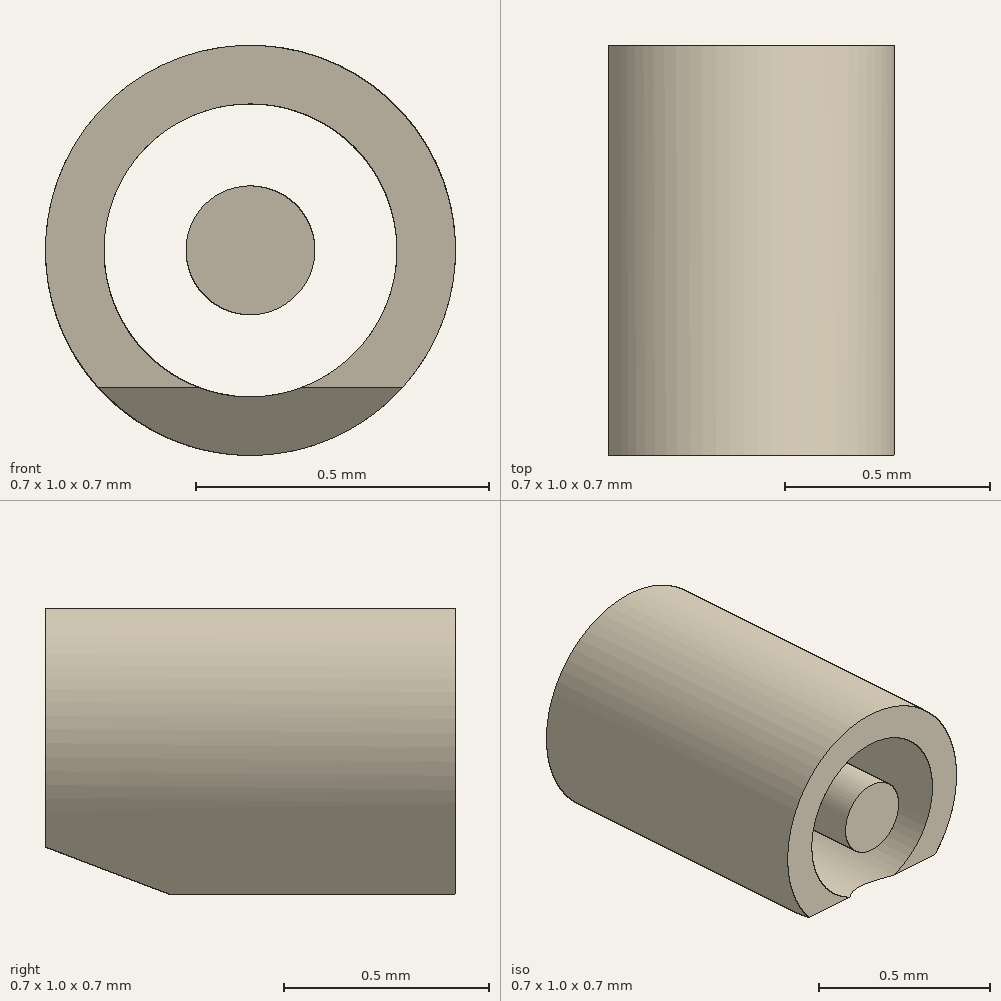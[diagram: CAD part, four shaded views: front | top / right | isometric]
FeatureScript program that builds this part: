
annotation { "Feature Type Name" : "Feature", "Feature Type Description" : "" }
export const myFeature = defineFeature(function(context is Context, id is Id, definition is map)
    precondition{}
    {
        {
            var Q0;
            Q0=qCreatedBy(makeId("Front.planeOp"),FACE);
            var sketch = newSketch(context, id + "F0", { "sketchPlane" : qUnion([Q0])});
            skCircle(sketch, "E0", {"center": v(0, 0) * mm, "radius": 0.11 * mm});
            skCircle(sketch, "E1", {"center": v(0, 0) * mm, "radius": 0.25 * mm});
            skCircle(sketch, "E2", {"center": v(0, 0) * mm, "radius": 0.35 * mm});
            skSolve(sketch);
        }
        {
            var Q0;
            Q0=makeQuery(id+"F0.imprint","IMPRINT",FACE,{"disambiguationData":[TD([[makeQuery(id+"F0.imprint","IMPRINT",EDGE,{"derivedFrom":sQuery(id+"F0.wireOp",EDGE,"E1")}),-1.0]])]});
            var Q1;
            Q1=makeQuery(id+"F0.imprint","IMPRINT",FACE,{"disambiguationData":[TD([[makeQuery(id+"F0.imprint","IMPRINT",EDGE,{"derivedFrom":sQuery(id+"F0.wireOp",EDGE,"E0")}),1.0]])]});
            extrude(context, id + "F1", {"entities" : qUnion([Q0, Q1]), "oppositeDirection" : true, "depth" : 1 * mm, "offsetDistance" : 25 * mm});
        }
        {
            var Q0;
            Q0=qCreatedBy(makeId("Top.planeOp"),FACE);
            var sketch = newSketch(context, id + "F2", { "sketchPlane" : qUnion([Q0])});
            skLineSegment(sketch, "E3", {"start": v(0.35, 0) * mm, "end": v(0.35, 1) * mm});
            skLineSegment(sketch, "E4", {"start": v(-0.35, 1) * mm, "end": v(-0.35, 0) * mm});
            skLineSegment(sketch, "E5", {"start": v(0.11, 0) * mm, "end": v(0.11, 1) * mm});
            skLineSegment(sketch, "E6", {"start": v(-0.11, 1) * mm, "end": v(-0.11, 0) * mm});
            skLineSegment(sketch, "E7", {"start": v(0, 0.93) * mm, "end": v(0, -1.02) * mm});
            skLineSegment(sketch, "E8", {"start": v(0.25, 0) * mm, "end": v(0.25, 1) * mm});
            skLineSegment(sketch, "E9", {"start": v(-0.25, 1) * mm, "end": v(-0.25, 0) * mm});
            skLineSegment(sketch, "E10", {"start": v(-0.11, 0) * mm, "end": v(0, -0.4) * mm});
            skLineSegment(sketch, "E11", {"start": v(0, -0.4) * mm, "end": v(0, -0.4) * mm});
            skLineSegment(sketch, "E12", {"start": v(0.1, 0) * mm, "end": v(0, -0.4) * mm});
            skLineSegment(sketch, "E13", {"start": v(-1.83, -0.4) * mm, "end": v(1.75, -0.4) * mm, "construction": true});
            skLineSegment(sketch, "E14", {"start": v(0.25, 0) * mm, "end": v(0.35, 0) * mm});
            skLineSegment(sketch, "E15", {"start": v(-0.11, 0) * mm, "end": v(0.11, 0) * mm});
            skLineSegment(sketch, "E16.MirrorCS", {"start": v(-0.25, 0) * mm, "end": v(-0.35, 0) * mm});
            skLineSegment(sketch, "E17", {"start": v(-0.35, 0) * mm, "end": v(-0.15, 0) * mm});
            skLineSegment(sketch, "E18", {"start": v(-0.15, 0) * mm, "end": v(-0.03, -0.37) * mm});
            skLineSegment(sketch, "E19", {"start": v(-0.03, -0.37) * mm, "end": v(-0.08, -0.4) * mm});
            skLineSegment(sketch, "E20", {"start": v(-0.07, -0.4) * mm, "end": v(-0.35, 0) * mm});
            skLineSegment(sketch, "E21.MirrorCS", {"start": v(0.07, -0.4) * mm, "end": v(0.35, 0) * mm});
            skLineSegment(sketch, "E22.MirrorCS", {"start": v(0.03, -0.37) * mm, "end": v(0.08, -0.4) * mm});
            skLineSegment(sketch, "E23.MirrorCS", {"start": v(0.15, 0) * mm, "end": v(0.03, -0.37) * mm});
            skLineSegment(sketch, "E24.MirrorCS", {"start": v(0.35, 0) * mm, "end": v(0.15, 0) * mm});
            skSolve(sketch);
        }
        {
            var Q0;
            {var subQ1=sQuery(id+"F2.wireOp",EDGE,"E21.MirrorCS");Q0=makeQuery(id+"F2.imprint","IMPRINT",FACE,{"disambiguationData":[TD([[makeQuery(id+"F2.imprint","IMPRINT",EDGE,{"derivedFrom":subQ1}),1.0]])]});}
            var Q1;
            {var subQ0=sQuery(id+"F2.wireOp",EDGE,"E18");Q1=makeQuery(id+"F2.imprint","IMPRINT",FACE,{"disambiguationData":[TD([[makeQuery(id+"F2.imprint","IMPRINT",EDGE,{"derivedFrom":subQ0}),-1.0]])]});}
            extrude(context, id + "F3", {"entities" : qUnion([Q0, Q1]), "operationType" : NewBodyOperationType.ADD, "endBound" : BoundingType.SYMMETRIC, "depth" : 0.01 * mm, "offsetDistance" : 25 * mm});
        }
        {
            var Q0;
            {var subQ5=sQuery(id+"F2.wireOp",EDGE,"E12");Q0=makeQuery(id+"F2.imprint","IMPRINT",FACE,{"disambiguationData":[TD([[makeQuery(id+"F2.imprint","IMPRINT",EDGE,{"derivedFrom":subQ5}),-1.0]])]});}
            var Q1;
            Q1=sQuery(id+"F2.wireOp",EDGE,"E7");
            revolve(context, id + "F4", {"operationType" : NewBodyOperationType.ADD, "entities" : qUnion([Q0]), "axis" : qUnion([Q1]), "revolveType" : RevolveType.FULL});
        }
        {
            var Q0;
            Q0=qCreatedBy(makeId("Right.planeOp"),FACE);
            var sketch = newSketch(context, id + "F5", { "sketchPlane" : qUnion([Q0])});
            skLineSegment(sketch, "E25", {"start": v(-0.43, 0.02) * mm, "end": v(-0.17, -0.17) * mm});
            skPoint(sketch, "E26.0", {"position": v(-0.4, 0) * mm});
            skLineSegment(sketch, "E27", {"start": v(-0.17, -0.17) * mm, "end": v(0.4, -0.39) * mm});
            skLineSegment(sketch, "E28", {"start": v(0.4, -0.39) * mm, "end": v(0.07, -0.8) * mm});
            skLineSegment(sketch, "E29", {"start": v(0.07, -0.8) * mm, "end": v(-0.43, 0.02) * mm});
            skSolve(sketch);
        }
        {
            var Q0;
            Q0=qSketchRegion(id+"F5",true);
            extrude(context, id + "F6", {"entities" : qUnion([Q0]), "operationType" : NewBodyOperationType.REMOVE, "endBound" : BoundingType.SYMMETRIC, "oppositeDirection" : true, "depth" : 25 * mm, "offsetDistance" : 25 * mm});
        }
        {
            var Q0;
            {var subQ0=sQuery(id+"F2.wireOp",EDGE,"E17");var subQ1=sQuery(id+"F0.wireOp",EDGE,"E1");var subQ2=sQuery(id+"F0.wireOp",EDGE,"E2");Q0=makeQuery(id+"F3.boolean.opBoolean","SPLIT",FACE,{"disambiguationData":[TD([makeQuery(id+"F3.opExtrude","CAP_FACE",FACE,{"disambiguationData":[OSD([subQ0,sQuery(id+"F2.wireOp",EDGE,"E18"),sQuery(id+"F2.wireOp",EDGE,"E19"),sQuery(id+"F2.wireOp",EDGE,"E20")])],"isStart":false})])],"derivedFrom":makeQuery(id+"F1.opExtrude","CAP_FACE",FACE,{"disambiguationData":[OSD([subQ1,subQ2])],"isStart":true})});}
            var sketch = newSketch(context, id + "F7", { "sketchPlane" : qUnion([Q0])});
            skLineSegment(sketch, "E30.bottom", {"start": v(0.42, -0.47) * mm, "end": v(-0.42, -0.47) * mm});
            skLineSegment(sketch, "E30.top", {"start": v(0.42, 0.47) * mm, "end": v(-0.42, 0.47) * mm});
            skLineSegment(sketch, "E30.left", {"start": v(0.42, -0.47) * mm, "end": v(0.42, 0.47) * mm});
            skLineSegment(sketch, "E30.right", {"start": v(-0.42, -0.47) * mm, "end": v(-0.42, 0.47) * mm});
            skPoint(sketch, "E30.middle", {"position": v(0, 0) * mm});
            skSolve(sketch);
        }
        {
            var Q0;
            Q0=makeQuery(id+"F7.imprint","IMPRINT",FACE,{"disambiguationData":[TD([[makeQuery(id+"F7.imprint","IMPRINT",EDGE,{"derivedFrom":sQuery(id+"F7.wireOp",EDGE,"E30.bottom")}),-1.0]])]});
            extrude(context, id + "F8", {"entities" : qUnion([Q0]), "operationType" : NewBodyOperationType.REMOVE, "depth" : 25 * mm, "offsetDistance" : 25 * mm});
        }
    });
